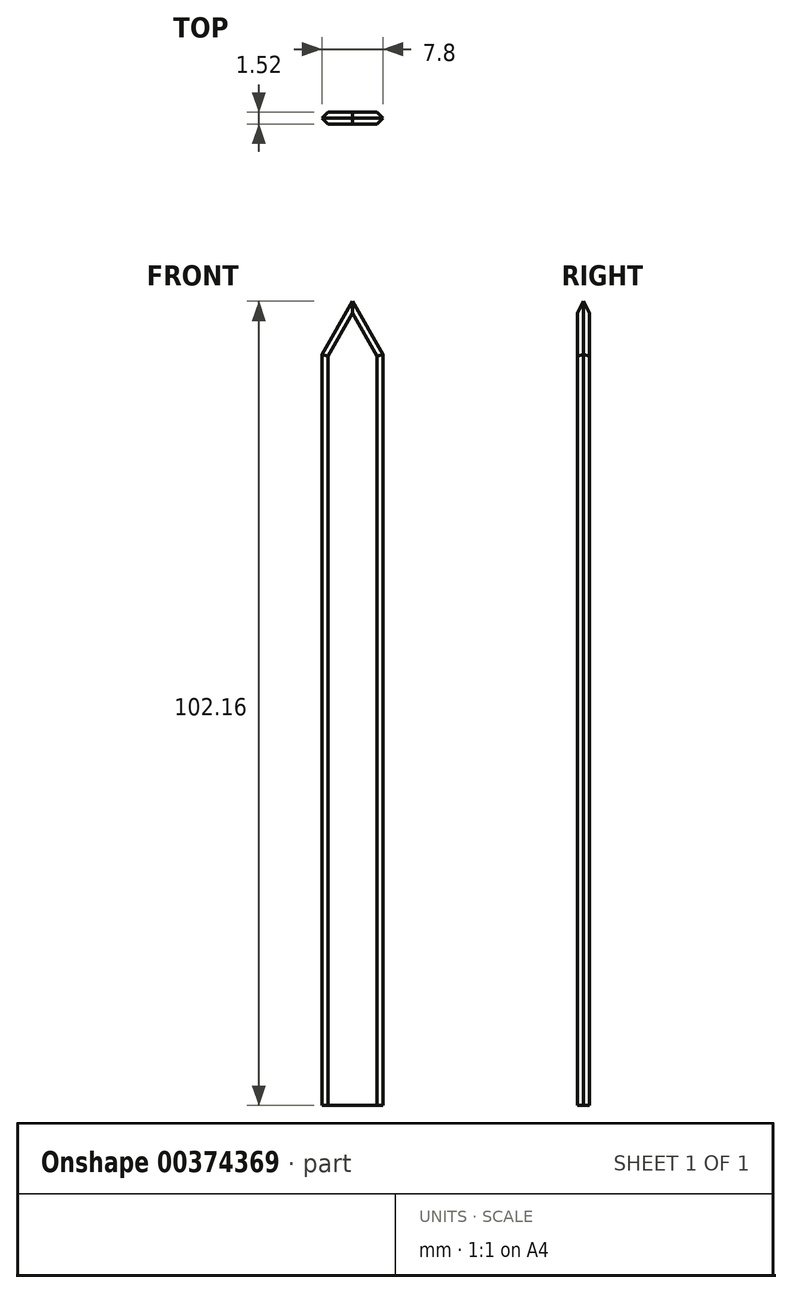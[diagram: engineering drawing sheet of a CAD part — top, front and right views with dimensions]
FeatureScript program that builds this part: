
annotation { "Feature Type Name" : "Feature", "Feature Type Description" : "" }
export const myFeature = defineFeature(function(context is Context, id is Id, definition is map)
    precondition{}
    {
        {
            var Q0;
            Q0=qCreatedBy(makeId("Front.planeOp"),FACE);
            var sketch = newSketch(context, id + "F0", { "sketchPlane" : qUnion([Q0])});
            skLineSegment(sketch, "E0.bottom", {"start": v(4.13, 47.53) * mm, "end": v(-4.13, 47.53) * mm});
            skLineSegment(sketch, "E0.top", {"start": v(4.13, -47.54) * mm, "end": v(-4.13, -47.54) * mm});
            skLineSegment(sketch, "E0.left", {"start": v(4.13, 47.53) * mm, "end": v(4.13, -47.54) * mm});
            skLineSegment(sketch, "E0.right", {"start": v(-4.13, 47.53) * mm, "end": v(-4.13, -47.54) * mm});
            skPoint(sketch, "E0.middle", {"position": v(0, 0) * mm});
            skLineSegment(sketch, "E1.bottom", {"start": v(1.32, -47.54) * mm, "end": v(-1.32, -47.54) * mm});
            skLineSegment(sketch, "E1.top", {"start": v(1.32, -70.57) * mm, "end": v(-1.32, -70.57) * mm});
            skLineSegment(sketch, "E1.left", {"start": v(1.32, -47.54) * mm, "end": v(1.32, -70.57) * mm});
            skLineSegment(sketch, "E1.right", {"start": v(-1.32, -47.54) * mm, "end": v(-1.32, -70.57) * mm});
            skPoint(sketch, "E1.middle", {"position": v(0, -59.05) * mm});
            skCircle(sketch, "E2.cCircle", {"center": v(0, 50.05) * mm, "radius": 2.52 * mm, "construction": true});
            skPoint(sketch, "E2.cCircle.centerSnap0", {"position": v(0, 47.53) * mm});
            skLineSegment(sketch, "E2.0", {"start": v(4.37, 47.53) * mm, "end": v(-4.37, 47.53) * mm});
            skLineSegment(sketch, "E2.1", {"start": v(-4.37, 47.53) * mm, "end": v(0, 55.1) * mm});
            skLineSegment(sketch, "E2.2", {"start": v(0, 55.1) * mm, "end": v(4.37, 47.53) * mm});
            skPoint(sketch, "E2.0.midPoint", {"position": v(0, 47.53) * mm});
            skSolve(sketch);
        }
        {
            var Q0;
            {var subQ0=sQuery(id+"F0.wireOp",EDGE,"E2.1");Q0=makeQuery(id+"F0.imprint","IMPRINT",FACE,{"disambiguationData":[TD([[makeQuery(id+"F0.imprint","IMPRINT",EDGE,{"derivedFrom":subQ0}),-1.0]])]});}
            var Q1;
            {var subQ1=sQuery(id+"F0.wireOp",EDGE,"E0.left");Q1=makeQuery(id+"F0.imprint","IMPRINT",FACE,{"disambiguationData":[TD([[makeQuery(id+"F0.imprint","IMPRINT",EDGE,{"derivedFrom":subQ1}),-1.0]])]});}
            var Q2;
            Q2=makeQuery(id+"F0.imprint","IMPRINT",FACE,{"disambiguationData":[TD([[makeQuery(id+"F0.imprint","IMPRINT",EDGE,{"derivedFrom":sQuery(id+"F0.wireOp",EDGE,"E1.bottom")}),1.0]])]});
            extrude(context, id + "F1", {"entities" : qUnion([Q0, Q1, Q2]), "depth" : 1.52 * mm});
        }
        {
            var Q0;
            Q0=makeQuery(id+"F1.opExtrude","CAP_EDGE",EDGE,{"disambiguationData":[OSD([sQuery(id+"F0.wireOp",EDGE,"E2.1")])],"isStart":false});
            chamfer(context, id + "F2", {"entities" : qUnion([Q0]), "width" : 1 * mm, "tangentPropagation" : true});
        }
        {
            var Q0;
            Q0=makeQuery(id+"F1.opExtrude","CAP_EDGE",EDGE,{"disambiguationData":[OSD([sQuery(id+"F0.wireOp",EDGE,"E2.2")])],"isStart":false});
            chamfer(context, id + "F3", {"entities" : qUnion([Q0]), "width" : 1 * mm, "tangentPropagation" : true});
        }
        {
            var Q0;
            Q0=makeQuery(id+"F1.opExtrude","CAP_EDGE",EDGE,{"disambiguationData":[OSD([sQuery(id+"F0.wireOp",EDGE,"E2.2")])],"isStart":true});
            chamfer(context, id + "F4", {"entities" : qUnion([Q0]), "width" : 1 * mm, "tangentPropagation" : true});
        }
        {
            var Q0;
            Q0=makeQuery(id+"F1.opExtrude","CAP_EDGE",EDGE,{"disambiguationData":[OSD([sQuery(id+"F0.wireOp",EDGE,"E2.1")])],"isStart":true});
            chamfer(context, id + "F5", {"entities" : qUnion([Q0]), "width" : 1 * mm, "tangentPropagation" : true});
        }
        {
            var Q0;
            Q0=makeQuery(id+"F1.opExtrude","CAP_EDGE",EDGE,{"disambiguationData":[OSD([sQuery(id+"F0.wireOp",EDGE,"E0.left")])],"isStart":false});
            chamfer(context, id + "F6", {"entities" : qUnion([Q0]), "width" : 1 * mm, "tangentPropagation" : true});
        }
        {
            var Q0;
            Q0=makeQuery(id+"F1.opExtrude","CAP_EDGE",EDGE,{"disambiguationData":[OSD([sQuery(id+"F0.wireOp",EDGE,"E0.left")])],"isStart":true});
            chamfer(context, id + "F7", {"entities" : qUnion([Q0]), "width" : 1 * mm, "tangentPropagation" : true});
        }
        {
            var Q0;
            Q0=makeQuery(id+"F1.opExtrude","CAP_EDGE",EDGE,{"disambiguationData":[OSD([sQuery(id+"F0.wireOp",EDGE,"E0.right")])],"isStart":true});
            chamfer(context, id + "F8", {"entities" : qUnion([Q0]), "width" : 1 * mm, "tangentPropagation" : true});
        }
        {
            var Q0;
            Q0=makeQuery(id+"F1.opExtrude","CAP_EDGE",EDGE,{"disambiguationData":[OSD([sQuery(id+"F0.wireOp",EDGE,"E0.right")])],"isStart":false});
            chamfer(context, id + "F9", {"entities" : qUnion([Q0]), "width" : 1 * mm, "tangentPropagation" : true});
        }
    });
